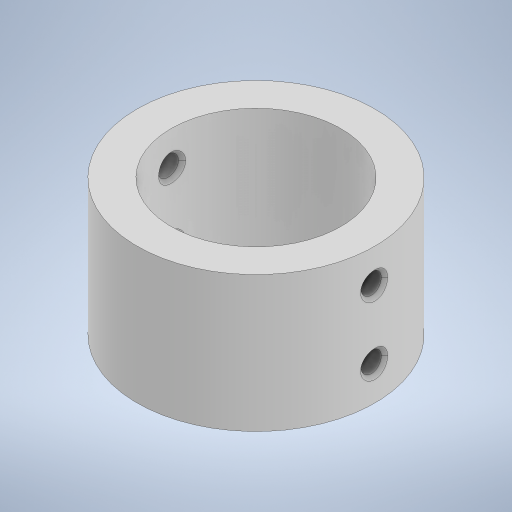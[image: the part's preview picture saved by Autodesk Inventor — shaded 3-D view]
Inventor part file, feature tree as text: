
AUTODESK INVENTOR PART (.ipt)
format: ipt  version: 2023 (Build 270158000, 158)  size: 302,080 bytes
history: native  units: mm
features: extrude x2, sketch x2, other x1, chamfer x1
ambient origin geometry x8: Origin, YZ Plane, XZ Plane, XY Plane, X Axis, Y Axis, Z Axis, Center Point
bodies: Body1 (feature_tree)
feature tree (6):
  other  "Твердое тело1"
  extrude  "Выдавливание1"  Depth=25.0mm
  extrude  "Выдавливание2"  Depth=35.0mm
  chamfer  "Фаска1"  Distance=20.0mm
  sketch  "Эскиз1"
  sketch  "Эскиз2"
